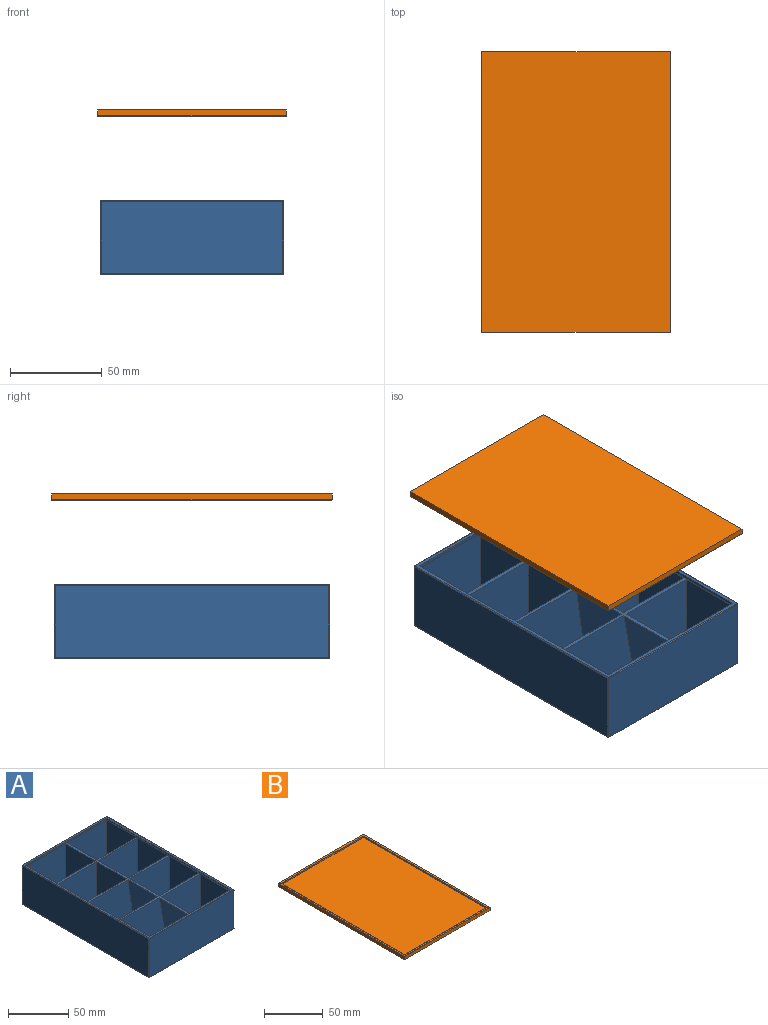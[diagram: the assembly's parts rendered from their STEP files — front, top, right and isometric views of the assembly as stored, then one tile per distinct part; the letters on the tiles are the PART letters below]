
ASSEMBLY  parts=2 mates=1
PART A: 81 faces, bbox 100x150x40 mm
  f0: plane 149.2x99.2mm, normal (0,0,1), area 881.3mm2, adj f9,f10,f19,f20,f27,f28,f29,f30
  f1: plane 99.2x39.2mm, normal (0,-1,0), area 3888.6mm2, adj f14,f19,f22,f25
  f2: plane 149.2x39.2mm, normal (1,0,0), area 5848.6mm2, adj f11,f20,f21,f25
  f3: plane 99.2x39.2mm, normal (0,1,0), area 3888.6mm2, adj f6,f10,f11,f12
  f4: plane 149.2x39.2mm, normal (-1,0,0), area 5848.6mm2, adj f6,f9,f13,f14
  f5: plane 149.2x99.2mm, normal (0,0,-1), area 14800.6mm2, adj f12,f13,f21,f22
  f6: cylinder r=0.4mm len=39.2mm, axis (0,0,1), area 24.6mm2, adj f3,f4,f7,f8
  f7: sphere r=0.4mm, area 0.3mm2, adj f6,f9,f10
  f8: sphere r=0.4mm, area 0.3mm2, adj f6,f12,f13
  f9: cylinder r=0.4mm len=149.2mm, axis (0,1,0), area 93.7mm2, adj f0,f4,f7,f15
  f10: cylinder r=0.4mm len=99.2mm, axis (1,0,0), area 62.3mm2, adj f0,f3,f7,f16
  f11: cylinder r=0.4mm len=39.2mm, axis (0,0,-1), area 24.6mm2, adj f2,f3,f16,f17
  f12: cylinder r=0.4mm len=99.2mm, axis (-1,0,0), area 62.3mm2, adj f3,f5,f8,f17
  f13: cylinder r=0.4mm len=149.2mm, axis (0,-1,0), area 93.7mm2, adj f4,f5,f8,f18
  f14: cylinder r=0.4mm len=39.2mm, axis (0,0,-1), area 24.6mm2, adj f1,f4,f15,f18
  f15: sphere r=0.4mm, area 0.3mm2, adj f9,f14,f19
  f16: sphere r=0.4mm, area 0.3mm2, adj f10,f11,f20
  f17: sphere r=0.4mm, area 0.3mm2, adj f11,f12,f21
  f18: sphere r=0.4mm, area 0.3mm2, adj f13,f14,f22
  f19: cylinder r=0.4mm len=99.2mm, axis (-1,0,0), area 62.3mm2, adj f0,f1,f15,f23
  f20: cylinder r=0.4mm len=149.2mm, axis (0,-1,0), area 93.7mm2, adj f0,f2,f16,f23
  f21: cylinder r=0.4mm len=149.2mm, axis (0,1,0), area 93.7mm2, adj f2,f5,f17,f24
  f22: cylinder r=0.4mm len=99.2mm, axis (1,0,0), area 62.3mm2, adj f1,f5,f18,f24
  f23: sphere r=0.4mm, area 0.3mm2, adj f19,f20,f25
  f24: sphere r=0.4mm, area 0.3mm2, adj f21,f22,f25
  f25: cylinder r=0.4mm len=39.2mm, axis (0,0,1), area 24.6mm2, adj f1,f2,f23,f24
  f26: plane 145.6x95.6mm, normal (0,0,1), area 1011.5mm2, adj f27,f28,f29,f30,f32,f33,f34,f35
  f27: plane 145.6x1.5mm, normal (-1,0,0), area 218.4mm2, adj f0,f26,f28,f30
  f28: plane 95.6x1.5mm, normal (0,-1,0), area 143.4mm2, adj f0,f26,f27,f29
  f29: plane 145.6x1.5mm, normal (1,0,0), area 218.4mm2, adj f0,f26,f28,f30
  f30: plane 95.6x1.5mm, normal (0,1,0), area 143.4mm2, adj f0,f26,f27,f29
  f31: plane 39.96x34.75mm, normal (0,0,1), area 1388.7mm2, adj f32,f33,f34,f35
  f32: plane 36x34.75mm, normal (0.98,0,0.17), area 1270.1mm2, adj f26,f31,f34,f35
  f33: plane 36x34.75mm, normal (-1,0,0), area 1251mm2, adj f26,f31,f34,f35
  f34: plane 46.27x36mm, normal (0,1,0), area 1552.3mm2, adj f26,f31,f32,f33
  f35: plane 46.27x36mm, normal (0,-1,0), area 1552.3mm2, adj f26,f31,f32,f33
  f36: plane 39.96x34.75mm, normal (0,0,1), area 1388.7mm2, adj f37,f38,f39,f40
  f37: plane 36x34.75mm, normal (0.98,0,0.17), area 1270.1mm2, adj f26,f36,f39,f40
  f38: plane 36x34.75mm, normal (-1,0,0), area 1251mm2, adj f26,f36,f39,f40
  f39: plane 46.27x36mm, normal (0,-1,0), area 1552.3mm2, adj f26,f36,f37,f38
  f40: plane 46.27x36mm, normal (0,1,0), area 1552.3mm2, adj f26,f36,f37,f38
  f41: plane 39.96x34.75mm, normal (0,0,1), area 1388.7mm2, adj f42,f43,f44,f45
  f42: plane 36x34.75mm, normal (0.98,0,0.17), area 1270.1mm2, adj f26,f41,f44,f45
  f43: plane 36x34.75mm, normal (-1,0,0), area 1251mm2, adj f26,f41,f44,f45
  f44: plane 46.27x36mm, normal (0,1,0), area 1552.3mm2, adj f26,f41,f42,f43
  f45: plane 46.27x36mm, normal (0,-1,0), area 1552.3mm2, adj f26,f41,f42,f43
  f46: plane 39.96x34.75mm, normal (0,0,1), area 1388.7mm2, adj f47,f48,f49,f50
  f47: plane 36x34.75mm, normal (0.98,0,0.17), area 1270.1mm2, adj f26,f46,f49,f50
  f48: plane 36x34.75mm, normal (-1,0,0), area 1251mm2, adj f26,f46,f49,f50
  f49: plane 46.27x36mm, normal (0,-1,0), area 1552.3mm2, adj f26,f46,f47,f48
  f50: plane 46.27x36mm, normal (0,1,0), area 1552.3mm2, adj f26,f46,f47,f48
  f51: plane 51.64x34.75mm, normal (0,0,1), area 1794.6mm2, adj f52,f53,f54,f55
  f52: plane 36x34.75mm, normal (-0.99,0,-0.14), area 1262.9mm2, adj f26,f51,f53,f55
  f53: plane 51.64x36mm, normal (0,1,0), area 1769.4mm2, adj f26,f51,f52,f54
  f54: plane 36x34.75mm, normal (1,0,0), area 1251mm2, adj f26,f51,f53,f55
  f55: plane 51.64x36mm, normal (0,-1,0), area 1769.4mm2, adj f26,f51,f52,f54
  f56: plane 46.5x34.75mm, normal (0,0,1), area 1615.9mm2, adj f57,f58,f59,f60
  f57: plane 46.5x36mm, normal (0,1,0), area 1674mm2, adj f26,f56,f59,f60
  f58: plane 46.5x36mm, normal (0,-1,0), area 1674mm2, adj f26,f56,f59,f60
  f59: plane 36x34.75mm, normal (-1,0,0), area 1251mm2, adj f26,f56,f57,f58
  f60: plane 36x34.75mm, normal (1,0,0), area 1251mm2, adj f26,f56,f57,f58
  f61: plane 46.5x34.75mm, normal (0,0,1), area 1615.9mm2, adj f62,f63,f64,f65
  f62: plane 46.5x36mm, normal (0,1,0), area 1674mm2, adj f26,f61,f63,f64
  f63: plane 36x34.75mm, normal (-1,0,0), area 1251mm2, adj f26,f61,f62,f65
  f64: plane 36x34.75mm, normal (1,0,0), area 1251mm2, adj f26,f61,f62,f65
  f65: plane 46.5x36mm, normal (0,-1,0), area 1674mm2, adj f26,f61,f63,f64
  f66: plane 53.01x34.75mm, normal (0,0,1), area 1842mm2, adj f67,f68,f69,f70
  f67: plane 36x34.75mm, normal (-0.98,0,-0.17), area 1270.1mm2, adj f26,f66,f68,f70
  f68: plane 53.01x36mm, normal (0,1,0), area 1794.6mm2, adj f26,f66,f67,f69
  f69: plane 36x34.75mm, normal (1,0,0), area 1251mm2, adj f26,f66,f68,f70
  f70: plane 53.01x36mm, normal (0,-1,0), area 1794.6mm2, adj f26,f66,f67,f69
  f71: plane 22.69x3.14mm, normal (0,1,0), area 35.7mm2, adj f73,f74,f75
  f72: plane 22.69x3.14mm, normal (0,-1,0), area 35.7mm2, adj f73,f74,f75
  f73: plane 34.75x22.69mm, normal (1,0,0), area 788.5mm2, adj f71,f72,f74,f75
  f74: plane 34.75x3.14mm, normal (0,0,1), area 109.2mm2, adj f71,f72,f73,f75
  f75: plane 34.75x22.69mm, normal (-0.99,0,-0.14), area 796.1mm2, adj f71,f72,f73,f74
  f76: plane 34.75x22.69mm, normal (-0.99,0,-0.14), area 796.1mm2, adj f77,f78,f79,f80
  f77: plane 22.69x3.14mm, normal (0,1,0), area 35.7mm2, adj f76,f78,f80
  f78: plane 34.75x22.69mm, normal (1,0,0), area 788.5mm2, adj f76,f77,f79,f80
  f79: plane 22.69x3.14mm, normal (0,-1,0), area 35.7mm2, adj f76,f78,f80
  f80: plane 34.75x3.14mm, normal (0,0,1), area 109.2mm2, adj f76,f77,f78,f79
PART B: 18 faces, bbox 103x153x3.4 mm
  f0: plane 152.8x102.6mm, normal (0,0,1), area 926.3mm2, adj f1,f11,f12,f13,f14,f15,f16,f17
  f1: plane 103x3.4mm, normal (0,1,0), area 350.2mm2, adj f0,f2,f4,f5,f15,f17
  f2: plane 153x3.2mm, normal (-1,0,0), area 489.6mm2, adj f1,f3,f5,f17
  f3: plane 103x3.2mm, normal (0,-1,0), area 329.6mm2, adj f2,f4,f5,f16
  f4: plane 153x3.2mm, normal (1,0,0), area 489.6mm2, adj f1,f3,f5,f15
  f5: plane 153x103mm, normal (0,0,-1), area 15759mm2, adj f1,f2,f3,f4
  f6: plane 100x1.4mm, normal (0,-1,0), area 140mm2, adj f7,f9,f10,f13
  f7: plane 150x1.4mm, normal (1,0,0), area 210mm2, adj f6,f8,f10,f11
  f8: plane 100x1.4mm, normal (0,1,0), area 140mm2, adj f7,f9,f10,f12
  f9: plane 150x1.4mm, normal (-1,0,0), area 210mm2, adj f6,f8,f10,f14
  f10: plane 150x100mm, normal (0,0,1), area 15000mm2, adj f6,f7,f8,f9
  f11: plane 150x0.5mm, normal (0.71,0,-0.71), area 105.7mm2, adj f0,f7,f12,f13
  f12: plane 100x0.5mm, normal (0,0.71,-0.71), area 70.4mm2, adj f0,f8,f11,f14
  f13: plane 100x0.5mm, normal (0,-0.71,-0.71), area 70.4mm2, adj f0,f6,f11,f14
  f14: plane 150x0.5mm, normal (-0.71,0,-0.71), area 105.7mm2, adj f0,f9,f12,f13
  f15: plane 153x0.2mm, normal (0.71,0,0.71), area 43.2mm2, adj f0,f1,f4,f16
  f16: plane 103x0.2mm, normal (0,-0.71,0.71), area 29.1mm2, adj f0,f3,f15,f17
  f17: plane 153x0.2mm, normal (-0.71,0,0.71), area 43.2mm2, adj f0,f1,f2,f16
PLACE A t=(74.52,-128.02,25.83)mm
PLACE B rot(axis=(0,-1,0),180deg) t=(-25.48,-128.02,113.91)mm
MATE slider B.f5 <-> A.f5  axis (0,0,1) through (24.52,-53.02,115.41)mm
